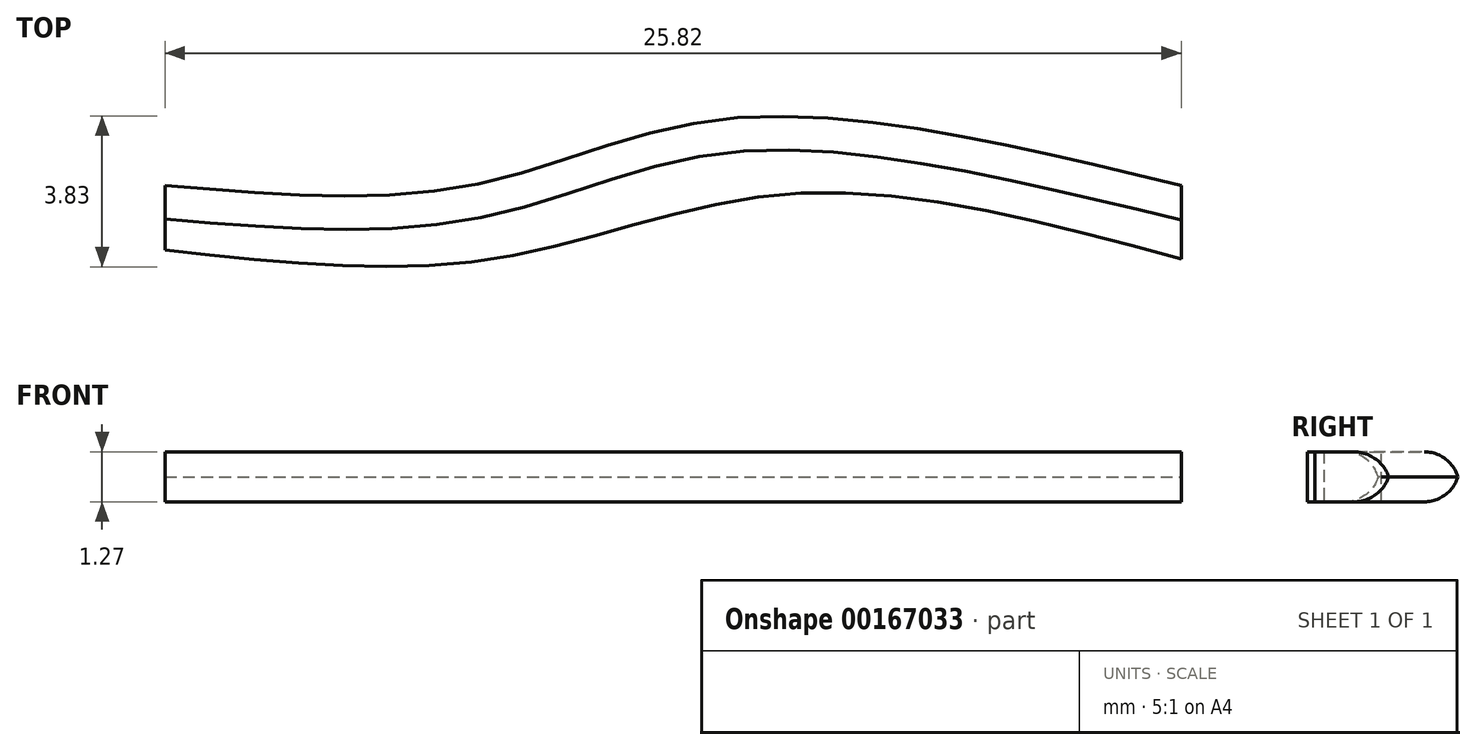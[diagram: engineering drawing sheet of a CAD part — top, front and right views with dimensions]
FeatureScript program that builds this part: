
annotation { "Feature Type Name" : "Feature", "Feature Type Description" : "" }
export const myFeature = defineFeature(function(context is Context, id is Id, definition is map)
    precondition{}
    {
        {
            var Q0;
            Q0=qCreatedBy(makeId("Top.planeOp"),FACE);
            var sketch = newSketch(context, id + "F0", { "sketchPlane" : qUnion([Q0])});
            skLineSegment(sketch, "E0", {"start": v(-23.26, 16.22) * mm, "end": v(-23.26, 14.55) * mm});
            skLineSegment(sketch, "E1", {"start": v(2.56, 16.22) * mm, "end": v(2.56, 14.32) * mm});
            skFitSpline(sketch, "E2", {"points": [v(-23.26, 16.22) * mm, v(-15.5, 16.22) * mm, v(-9, 17.92) * mm, v(2.56, 16.22) * mm], "startDerivative": vector(25.63, -2.17) * mm, "endDerivative": vector(32.26, -7.8) * mm});
            skPoint(sketch, "E3.2.internal.snap0", {"position": v(2.56, 14.32) * mm});
            skFitSpline(sketch, "E3", {"points": [v(2.56, 14.32) * mm, v(-7.39, 15.98) * mm, v(-14.93, 14.32) * mm, v(-23.26, 14.55) * mm], "startDerivative": vector(-28.85, 7.82) * mm, "endDerivative": vector(-26.15, 2.94) * mm});
            skPoint(sketch, "E4.1.internal.orphan", {"position": v(-15.36, 12.41) * mm});
            skPoint(sketch, "E4.3.internal.orphan", {"position": v(2.56, 12.41) * mm});
            skPoint(sketch, "E5.orphan", {"position": v(-23.26, 12.41) * mm});
            skSolve(sketch);
        }
        {
            var Q0;
            Q0=makeQuery(id+"F0.imprint","IMPRINT",FACE,{"disambiguationData":[TD([[makeQuery(id+"F0.imprint","IMPRINT",EDGE,{"derivedFrom":sQuery(id+"F0.wireOp",EDGE,"E0")}),1.0]])]});
            extrude(context, id + "F1", {"entities" : qUnion([Q0]), "depth" : 1.27 * mm});
        }
        {
            var Q0;
            Q0=makeQuery(id+"F1.opExtrude","CAP_EDGE",EDGE,{"disambiguationData":[OSD([sQuery(id+"F0.wireOp",EDGE,"E4")])],"isStart":false});
            var Q1;
            Q1=makeQuery(id+"F1.opExtrude","CAP_EDGE",EDGE,{"disambiguationData":[OSD([sQuery(id+"F0.wireOp",EDGE,"E4")])],"isStart":true});
            var Q2;
            Q2=makeQuery(id+"F1.opExtrude","CAP_EDGE",EDGE,{"disambiguationData":[OSD([sQuery(id+"F0.wireOp",EDGE,"E2")])],"isStart":false});
            var Q3;
            Q3=makeQuery(id+"F1.opExtrude","CAP_EDGE",EDGE,{"disambiguationData":[OSD([sQuery(id+"F0.wireOp",EDGE,"E2")])],"isStart":true});
            fillet(context, id + "F2", {"entities" : qUnion([Q0, Q1, Q2, Q3]), "radius" : 0.89 * mm, "tangentPropagation" : true, "allowEdgeOverflow" : false});
        }
    });
